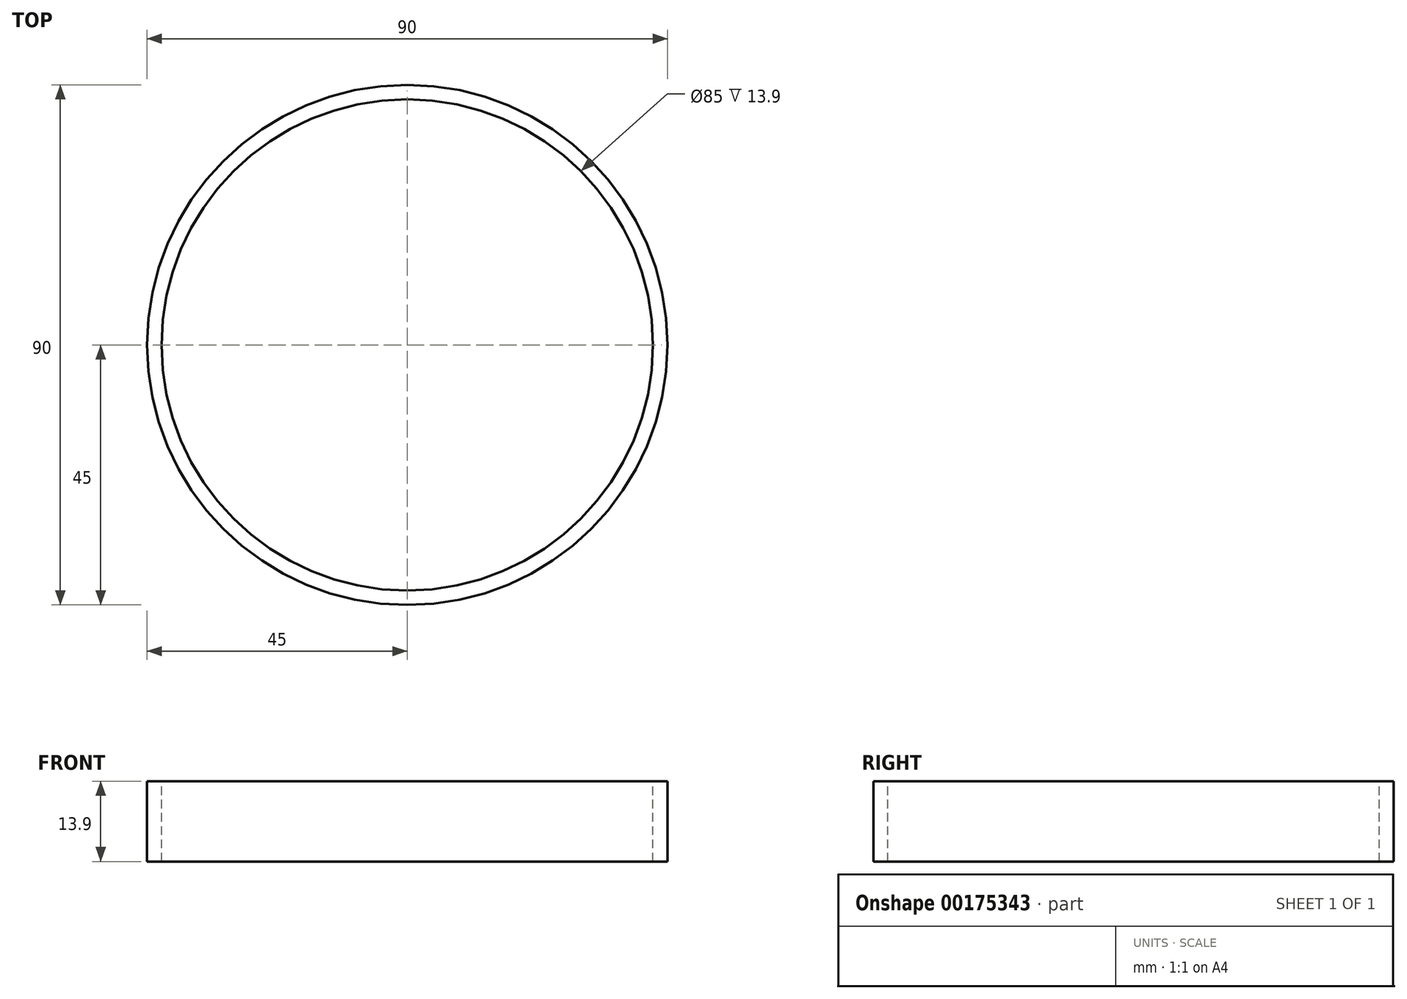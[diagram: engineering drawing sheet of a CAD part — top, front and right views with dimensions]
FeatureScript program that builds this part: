
annotation { "Feature Type Name" : "Feature", "Feature Type Description" : "" }
export const myFeature = defineFeature(function(context is Context, id is Id, definition is map)
    precondition{}
    {
        {
            var Q0;
            Q0=qCreatedBy(makeId("Front.planeOp"),FACE);
            var sketch = newSketch(context, id + "F0", { "sketchPlane" : qUnion([Q0])});
            skLineSegment(sketch, "E0.bottom", {"start": v(-1, 6.95) * mm, "end": v(1.5, 6.95) * mm});
            skLineSegment(sketch, "E0.top", {"start": v(-1, -6.95) * mm, "end": v(1.5, -6.95) * mm});
            skLineSegment(sketch, "E0.left", {"start": v(-1, 6.95) * mm, "end": v(-1, -6.95) * mm});
            skLineSegment(sketch, "E0.right", {"start": v(1.5, 6.95) * mm, "end": v(1.5, -6.95) * mm});
            skLineSegment(sketch, "E1", {"start": v(44, 14.03) * mm, "end": v(44, -16.41) * mm, "construction": true});
            skSolve(sketch);
        }
        {
            var Q0;
            Q0 = qSketchRegion(id + "F0", true);
            var Q1;
            Q1=sQuery(id+"F0.wireOp",EDGE,"E1");
            revolve(context, id + "F1", {"entities" : qUnion([Q0]), "axis" : qUnion([Q1]), "revolveType" : RevolveType.FULL});
        }
    });
